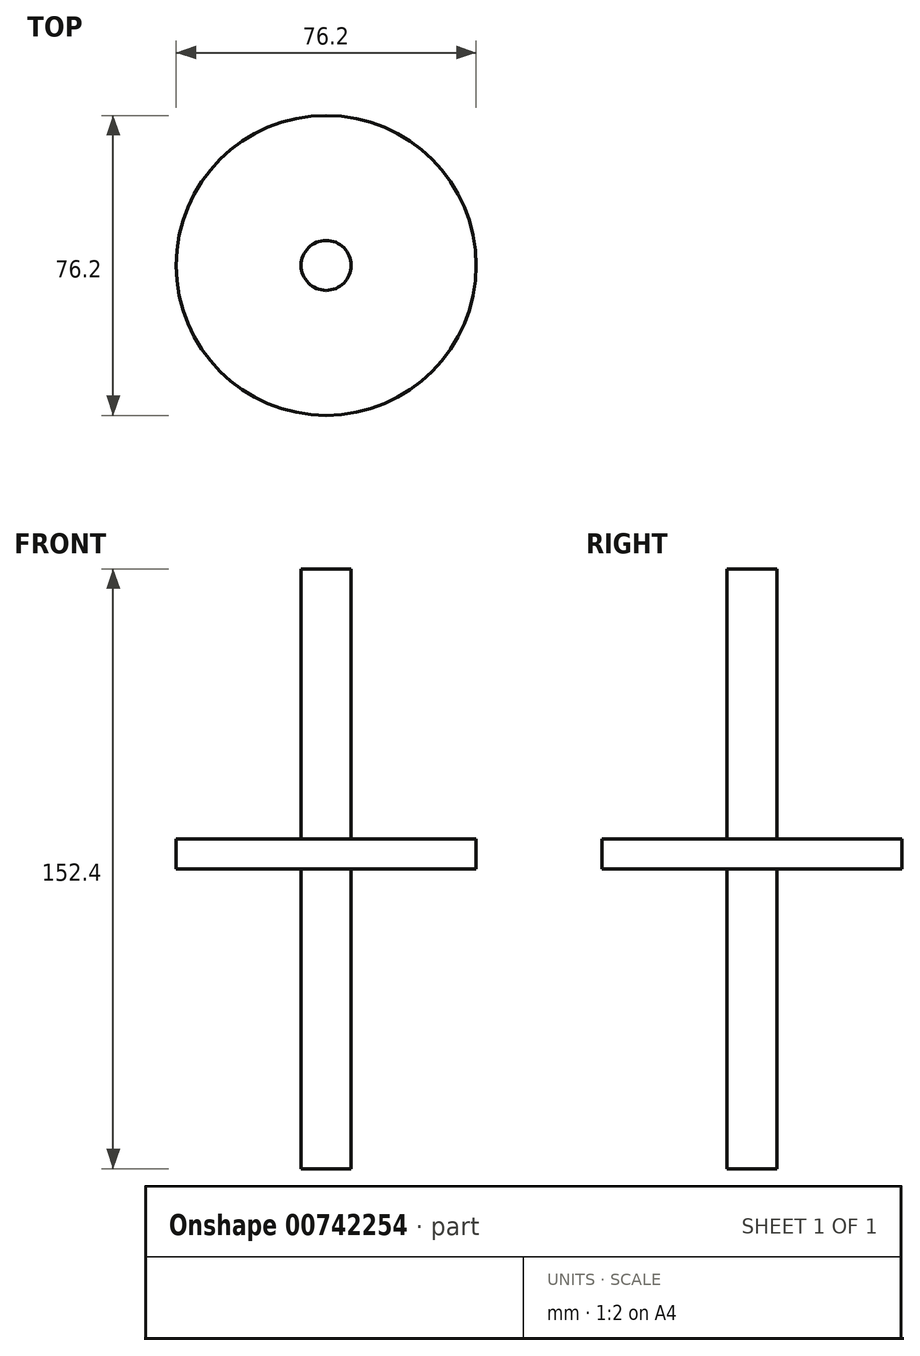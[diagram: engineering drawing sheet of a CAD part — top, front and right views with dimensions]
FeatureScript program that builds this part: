
annotation { "Feature Type Name" : "Feature", "Feature Type Description" : "" }
export const myFeature = defineFeature(function(context is Context, id is Id, definition is map)
    precondition{}
    {
        {
            var Q0;
            Q0=qCreatedBy(makeId("Top.planeOp"),FACE);
            var sketch = newSketch(context, id + "F0", { "sketchPlane" : qUnion([Q0])});
            skCircle(sketch, "E0", {"center": v(0, 0) * mm, "radius": 38.1 * mm});
            skSolve(sketch);
        }
        {
            var Q0;
            Q0=makeQuery(id+"F0.imprint","IMPRINT",FACE,{"disambiguationData":[TD([[makeQuery(id+"F0.imprint","IMPRINT",EDGE,{"derivedFrom":sQuery(id+"F0.wireOp",EDGE,"E0")}),1.0]])]});
            var Q1;
            Q1=sQuery(id+"F0.wireOp",EDGE,"E0");
            extrude(context, id + "F1", {"entities" : qUnion([Q0]), "surfaceEntities" : qUnion([Q1]), "depth" : 7.62 * mm, "offsetDistance" : 25.4 * mm});
        }
        {
            var Q0;
            Q0=qCreatedBy(makeId("Top.planeOp"),FACE);
            var sketch = newSketch(context, id + "F2", { "sketchPlane" : qUnion([Q0])});
            skCircle(sketch, "E1", {"center": v(0, 0) * mm, "radius": 6.35 * mm});
            skSolve(sketch);
        }
        {
            var Q0;
            Q0=sQuery(id+"F2.wireOp",VERTEX,"E1.center");
            var Q1;
            Q1=makeQuery(id+"F1.opExtrude","SWEPT_BODY",BODY,{"disambiguationData":[OSD([sQuery(id+"F0.wireOp",EDGE,"E0")])]});
            hole(context, id + "F3", {"style" : HoleStyle.SIMPLE, "endStyle" : HoleEndStyle.THROUGH, "oppositeDirection" : true, "holeDiameter" : 12.7 * mm, "majorDiameter" : 6.35 * mm, "isTappedThrough" : true, "tappedDepth" : 12.7 * mm, "tapClearance" : 3, "locations" : qUnion([Q0]), "scope" : qUnion([Q1])});
        }
        {
            var Q0;
            Q0=qCreatedBy(makeId("Top.planeOp"),FACE);
            var sketch = newSketch(context, id + "F4", { "sketchPlane" : qUnion([Q0])});
            skCircle(sketch, "E2", {"center": v(0, 0) * mm, "radius": 6.35 * mm});
            skSolve(sketch);
        }
        {
            var Q0;
            Q0=makeQuery(id+"F4.imprint","IMPRINT",FACE,{"disambiguationData":[TD([[makeQuery(id+"F4.imprint","IMPRINT",EDGE,{"derivedFrom":sQuery(id+"F4.wireOp",EDGE,"E2")}),1.0]])]});
            extrude(context, id + "F5", {"entities" : qUnion([Q0]), "operationType" : NewBodyOperationType.ADD, "depth" : 76.2 * mm, "offsetDistance" : 25.4 * mm, "hasSecondDirection" : true, "secondDirectionOppositeDirection" : true, "secondDirectionDepth" : 76.2 * mm});
        }
    });
